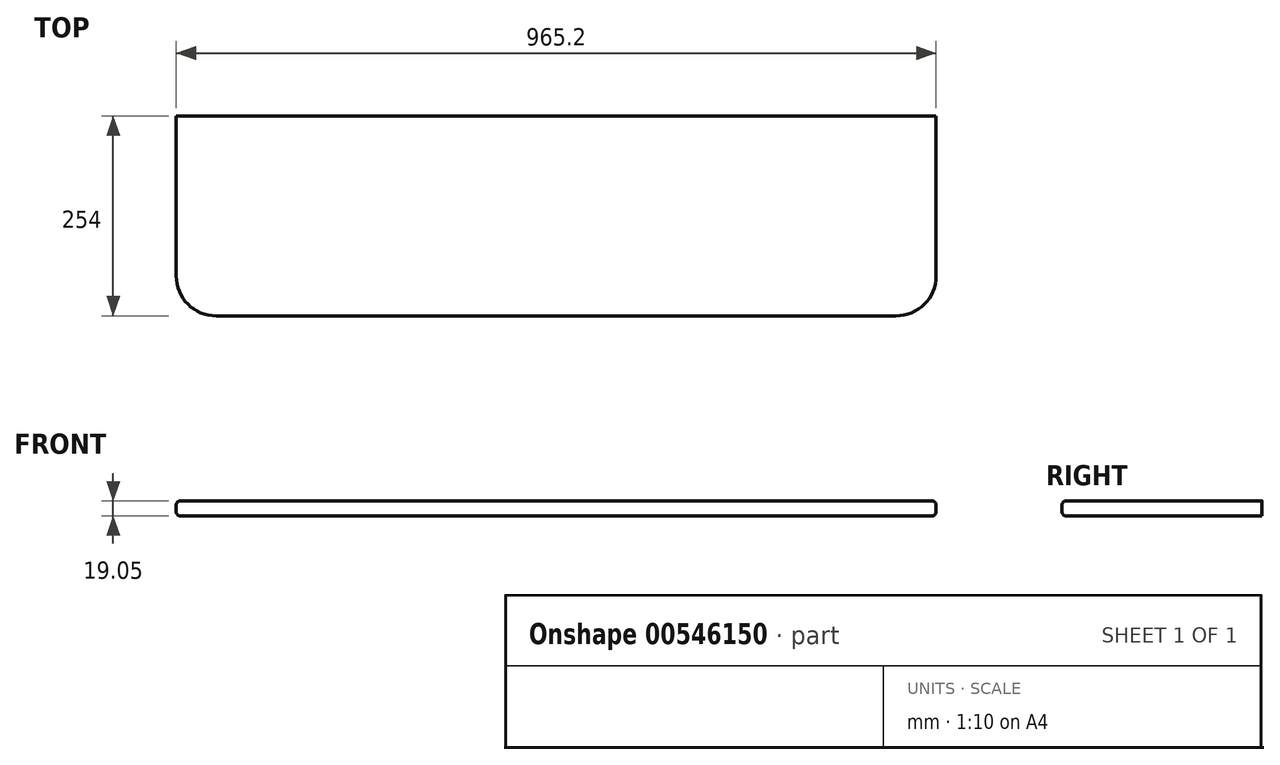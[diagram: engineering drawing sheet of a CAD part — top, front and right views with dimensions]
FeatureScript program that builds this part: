
annotation { "Feature Type Name" : "Feature", "Feature Type Description" : "" }
export const myFeature = defineFeature(function(context is Context, id is Id, definition is map)
    precondition{}
    {
        {
            var Q0;
            Q0=qCreatedBy(makeId("Top.planeOp"),FACE);
            var sketch = newSketch(context, id + "F0", { "sketchPlane" : qUnion([Q0])});
            skLineSegment(sketch, "E0.bottom", {"start": v(-482.6, 127) * mm, "end": v(482.6, 127) * mm});
            skLineSegment(sketch, "E0.top", {"start": v(-431.8, -127) * mm, "end": v(431.8, -127) * mm});
            skLineSegment(sketch, "E0.left", {"start": v(-482.6, 127) * mm, "end": v(-482.6, -76.2) * mm});
            skLineSegment(sketch, "E0.right", {"start": v(482.6, 127) * mm, "end": v(482.6, -76.2) * mm});
            skPoint(sketch, "E0.middle", {"position": v(0, 0) * mm});
            skPoint(sketch, "E1.visualSharp", {"position": v(-482.6, -127) * mm});
            skArc(sketch, "E1.filletArc", {"start": v(-482.6, -76.2) * mm, "mid": v(-467.72, -112.12) * mm, "end": v(-431.8, -127) * mm});
            skPoint(sketch, "E2.visualSharp", {"position": v(482.6, -127) * mm});
            skArc(sketch, "E2.filletArc", {"start": v(431.8, -127) * mm, "mid": v(467.72, -112.12) * mm, "end": v(482.6, -76.2) * mm});
            skSolve(sketch);
        }
        {
            var Q0;
            Q0=makeQuery(id+"F0.imprint","IMPRINT",FACE,{"disambiguationData":[TD([[makeQuery(id+"F0.imprint","IMPRINT",EDGE,{"derivedFrom":sQuery(id+"F0.wireOp",EDGE,"E0.bottom")}),-1.0]])]});
            extrude(context, id + "F1", {"entities" : qUnion([Q0]), "depth" : 19.05 * mm, "offsetDistance" : 25.4 * mm});
        }
        {
            var Q0;
            Q0=makeQuery(id+"F1.opExtrude","CAP_EDGE",EDGE,{"disambiguationData":[OSD([sQuery(id+"F0.wireOp",EDGE,"E0.top")])],"isStart":false});
            fillet(context, id + "F2", {"entities" : qUnion([Q0]), "radius" : 5.08 * mm, "tangentPropagation" : true, "allowEdgeOverflow" : false});
        }
        {
            var Q0;
            Q0=makeQuery(id+"F1.opExtrude","CAP_EDGE",EDGE,{"disambiguationData":[OSD([sQuery(id+"F0.wireOp",EDGE,"E0.top")])],"isStart":true});
            fillet(context, id + "F3", {"entities" : qUnion([Q0]), "radius" : 5.08 * mm, "tangentPropagation" : true, "allowEdgeOverflow" : false});
        }
    });
